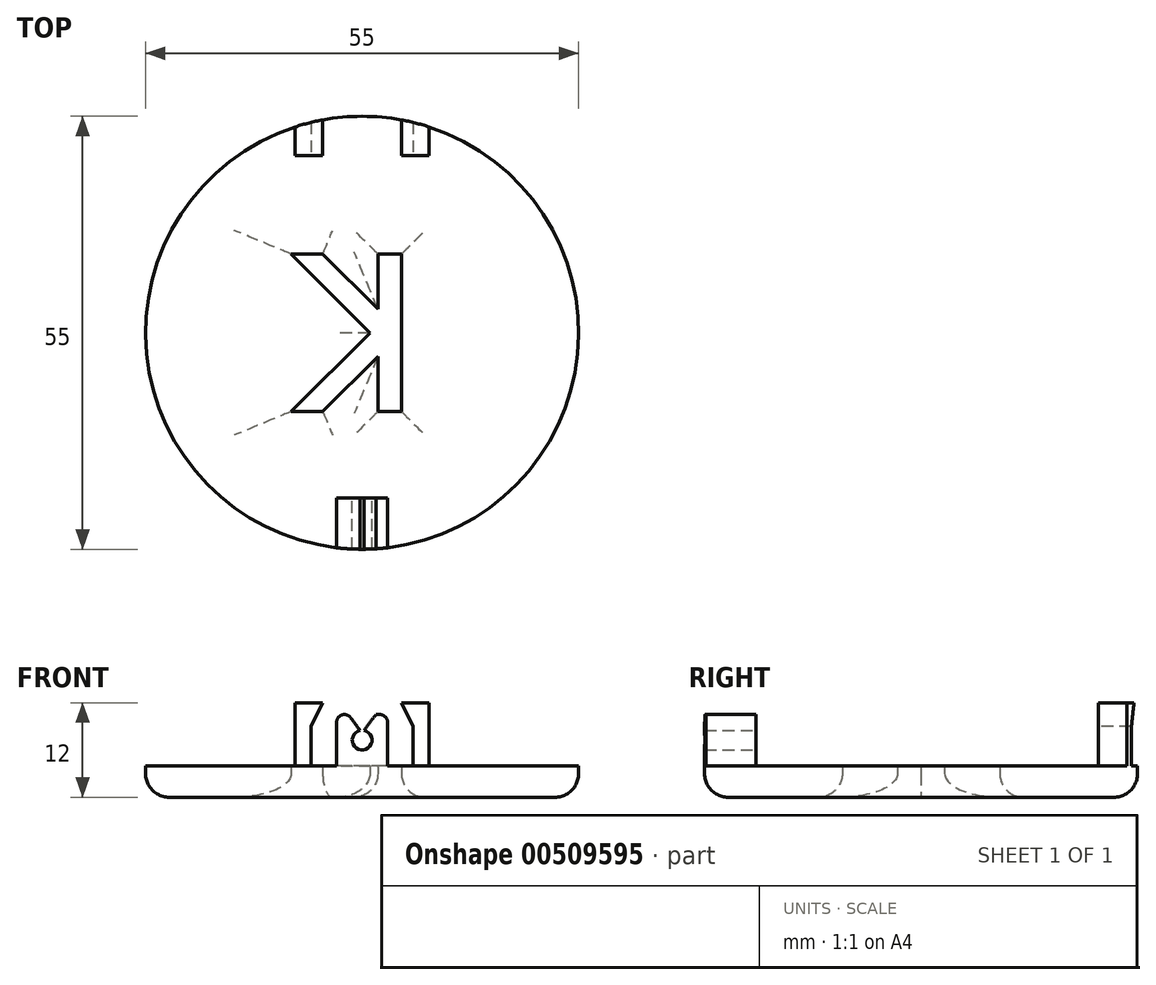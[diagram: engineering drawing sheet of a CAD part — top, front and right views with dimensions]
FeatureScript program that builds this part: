
annotation { "Feature Type Name" : "Feature", "Feature Type Description" : "" }
export const myFeature = defineFeature(function(context is Context, id is Id, definition is map)
    precondition{}
    {
        {
            var Q0;
            Q0=qCreatedBy(makeId("Top.planeOp"),FACE);
            var sketch = newSketch(context, id + "F0", { "sketchPlane" : qUnion([Q0])});
            skCircle(sketch, "E0", {"center": v(0, 0) * mm, "radius": 27.5 * mm});
            skSolve(sketch);
        }
        {
            var Q0;
            Q0=makeQuery(id+"F0.imprint","IMPRINT",FACE,{"disambiguationData":[TD([[makeQuery(id+"F0.imprint","IMPRINT",EDGE,{"derivedFrom":sQuery(id+"F0.wireOp",EDGE,"E0")}),1.0]])]});
            extrude(context, id + "F1", {"entities" : qUnion([Q0]), "depth" : 4 * mm});
        }
        {
            var Q0;
            Q0=makeQuery(id+"F1.opExtrude","CAP_FACE",FACE,{"disambiguationData":[OSD([sQuery(id+"F0.wireOp",EDGE,"E0")])],"isStart":false});
            var sketch = newSketch(context, id + "F2", { "sketchPlane" : qUnion([Q0])});
            skLineSegment(sketch, "E1.bottom", {"start": v(8.5, 27.5) * mm, "end": v(-8.5, 27.5) * mm});
            skLineSegment(sketch, "E1.top", {"start": v(8.5, 22.5) * mm, "end": v(-8.5, 22.5) * mm});
            skLineSegment(sketch, "E1.left", {"start": v(8.5, 27.5) * mm, "end": v(8.5, 22.5) * mm});
            skLineSegment(sketch, "E1.right", {"start": v(-8.5, 27.5) * mm, "end": v(-8.5, 22.5) * mm});
            skPoint(sketch, "E1.middle", {"position": v(0, 25) * mm});
            skSolve(sketch);
        }
        {
            var Q0;
            {var subQ5=sQuery(id+"F2.wireOp",EDGE,"E1.top");Q0=makeQuery(id+"F2.imprint","IMPRINT",FACE,{"disambiguationData":[TD([[makeQuery(id+"F2.imprint","IMPRINT",EDGE,{"derivedFrom":subQ5}),-1.0]])]});}
            extrude(context, id + "F3", {"entities" : qUnion([Q0]), "operationType" : NewBodyOperationType.ADD, "depth" : 8 * mm});
        }
        {
            var Q0;
            Q0=makeQuery(id+"F3.opExtrude","SWEPT_FACE",FACE,{"disambiguationData":[OSD([sQuery(id+"F2.wireOp",EDGE,"E1.top")])]});
            var sketch = newSketch(context, id + "F4", { "sketchPlane" : qUnion([Q0])});
            skLineSegment(sketch, "E2.bottom", {"start": v(6.5, 9) * mm, "end": v(-6.5, 9) * mm});
            skLineSegment(sketch, "E2.top", {"start": v(6.5, 4) * mm, "end": v(-6.5, 4) * mm});
            skLineSegment(sketch, "E2.left", {"start": v(6.5, 9) * mm, "end": v(6.5, 4) * mm});
            skLineSegment(sketch, "E2.right", {"start": v(-6.5, 9) * mm, "end": v(-6.5, 4) * mm});
            skPoint(sketch, "E2.middle", {"position": v(0, 6.5) * mm});
            skSolve(sketch);
        }
        {
            var Q0;
            Q0=makeQuery(id+"F4.imprint","IMPRINT",FACE,{"disambiguationData":[TD([[makeQuery(id+"F4.imprint","IMPRINT",EDGE,{"derivedFrom":sQuery(id+"F4.wireOp",EDGE,"E2.bottom")}),1.0]])]});
            extrude(context, id + "F5", {"entities" : qUnion([Q0]), "operationType" : NewBodyOperationType.REMOVE, "oppositeDirection" : true, "depth" : 25 * mm});
        }
        {
            var Q0;
            Q0=makeQuery(id+"F3.opExtrude","SWEPT_FACE",FACE,{"disambiguationData":[OSD([sQuery(id+"F2.wireOp",EDGE,"E1.top")])]});
            var sketch = newSketch(context, id + "F6", { "sketchPlane" : qUnion([Q0])});
            skLineSegment(sketch, "E3.bottom", {"start": v(5, 12) * mm, "end": v(-5, 12) * mm});
            skLineSegment(sketch, "E3.top", {"start": v(5, 9) * mm, "end": v(-5, 9) * mm});
            skLineSegment(sketch, "E3.left", {"start": v(5, 12) * mm, "end": v(5, 9) * mm});
            skLineSegment(sketch, "E3.right", {"start": v(-5, 12) * mm, "end": v(-5, 9) * mm});
            skPoint(sketch, "E3.middle", {"position": v(0, 10.5) * mm});
            skSolve(sketch);
        }
        {
            var Q0;
            Q0=makeQuery(id+"F6.imprint","IMPRINT",FACE,{"disambiguationData":[TD([[makeQuery(id+"F6.imprint","IMPRINT",EDGE,{"derivedFrom":sQuery(id+"F6.wireOp",EDGE,"E3.bottom")}),1.0]])]});
            extrude(context, id + "F7", {"entities" : qUnion([Q0]), "operationType" : NewBodyOperationType.REMOVE, "oppositeDirection" : true, "depth" : 25 * mm});
        }
        {
            var Q0;
            {var subQ0=sQuery(id+"F2.wireOp",EDGE,"E1.right");var subQ1=sQuery(id+"F2.wireOp",EDGE,"E1.top");Q0=makeQuery(id+"F7.boolean.opBoolean","SPLIT",FACE,{"disambiguationData":[TD([makeQuery(id+"F3.opExtrude","SWEPT_FACE",FACE,{"disambiguationData":[OSD([subQ0])]})])],"derivedFrom":makeQuery(id+"F3.opExtrude","SWEPT_FACE",FACE,{"disambiguationData":[OSD([subQ1])]})});}
            var sketch = newSketch(context, id + "F8", { "sketchPlane" : qUnion([Q0])});
            skLineSegment(sketch, "E4", {"start": v(-6.5, 9) * mm, "end": v(-5, 12) * mm});
            skSolve(sketch);
        }
        {
            var Q0;
            Q0=makeQuery(id+"F8.imprint","IMPRINT",FACE,{"disambiguationData":[TD([[makeQuery(id+"F8.imprint","IMPRINT",EDGE,{"derivedFrom":sQuery(id+"F8.wireOp",EDGE,"E4")}),-1.0]])]});
            extrude(context, id + "F9", {"entities" : qUnion([Q0]), "operationType" : NewBodyOperationType.REMOVE, "oppositeDirection" : true, "depth" : 25 * mm});
        }
        {
            var Q0;
            {var subQ0=sQuery(id+"F2.wireOp",EDGE,"E1.left");var subQ1=sQuery(id+"F2.wireOp",EDGE,"E1.top");Q0=makeQuery(id+"F7.boolean.opBoolean","SPLIT",FACE,{"disambiguationData":[TD([makeQuery(id+"F3.opExtrude","SWEPT_FACE",FACE,{"disambiguationData":[OSD([subQ0])]})])],"derivedFrom":makeQuery(id+"F3.opExtrude","SWEPT_FACE",FACE,{"disambiguationData":[OSD([subQ1])]})});}
            var sketch = newSketch(context, id + "F10", { "sketchPlane" : qUnion([Q0])});
            skLineSegment(sketch, "E5", {"start": v(6.5, 9) * mm, "end": v(5, 12) * mm});
            skSolve(sketch);
        }
        {
            var Q0;
            Q0=makeQuery(id+"F10.imprint","IMPRINT",FACE,{"disambiguationData":[TD([[makeQuery(id+"F10.imprint","IMPRINT",EDGE,{"derivedFrom":sQuery(id+"F10.wireOp",EDGE,"E5")}),1.0]])]});
            extrude(context, id + "F11", {"entities" : qUnion([Q0]), "operationType" : NewBodyOperationType.REMOVE, "oppositeDirection" : true, "depth" : 25 * mm});
        }
        {
            var Q0;
            Q0=makeQuery(id+"F5.boolean.opBoolean","MERGE",FACE,{"derivedFrom":[makeQuery(id+"F1.opExtrude","CAP_FACE",FACE,{"disambiguationData":[OSD([sQuery(id+"F0.wireOp",EDGE,"E0")])],"isStart":false}),makeQuery(id+"F5.opExtrude","SWEPT_FACE",FACE,{"disambiguationData":[OSD([sQuery(id+"F4.wireOp",EDGE,"E2.top")])]})]});
            var sketch = newSketch(context, id + "F12", { "sketchPlane" : qUnion([Q0])});
            skLineSegment(sketch, "E6.bottom", {"start": v(3.25, -21) * mm, "end": v(-3.25, -21) * mm});
            skLineSegment(sketch, "E6.top", {"start": v(3.25, -27.5) * mm, "end": v(-3.25, -27.5) * mm});
            skLineSegment(sketch, "E6.left", {"start": v(3.25, -21) * mm, "end": v(3.25, -27.5) * mm});
            skLineSegment(sketch, "E6.right", {"start": v(-3.25, -21) * mm, "end": v(-3.25, -27.5) * mm});
            skPoint(sketch, "E6.middle", {"position": v(0, -24.25) * mm});
            skPoint(sketch, "E6.middle.positionSnap0", {"position": v(0, -27.5) * mm});
            skPoint(sketch, "E6.centerSnap0", {"position": v(0, -27.5) * mm});
            skSolve(sketch);
        }
        {
            var Q0;
            {var subQ5=sQuery(id+"F12.wireOp",EDGE,"E6.bottom");Q0=makeQuery(id+"F12.imprint","IMPRINT",FACE,{"disambiguationData":[TD([[makeQuery(id+"F12.imprint","IMPRINT",EDGE,{"derivedFrom":subQ5}),1.0]])]});}
            extrude(context, id + "F13", {"entities" : qUnion([Q0]), "operationType" : NewBodyOperationType.ADD, "depth" : 6.5 * mm});
        }
        {
            var Q0;
            Q0=makeQuery(id+"F13.opExtrude","SWEPT_FACE",FACE,{"disambiguationData":[OSD([sQuery(id+"F12.wireOp",EDGE,"E6.bottom")])]});
            var sketch = newSketch(context, id + "F14", { "sketchPlane" : qUnion([Q0])});
            skPoint(sketch, "E7", {"position": v(0, 7.25) * mm});
            skSolve(sketch);
        }
        {
            var Q0;
            Q0=sQuery(id+"F14.wireOp",VERTEX,"E7");
            var Q1;
            Q1=makeQuery(id+"F1.opExtrude","SWEPT_BODY",BODY,{"disambiguationData":[OSD([sQuery(id+"F0.wireOp",EDGE,"E0")])]});
            hole(context, id + "F15", {"style" : HoleStyle.SIMPLE, "endStyle" : HoleEndStyle.THROUGH, "holeDiameter" : 2.5 * mm, "isTappedThrough" : true, "tappedDepth" : 12 * mm, "tapClearance" : 3, "locations" : qUnion([Q0]), "scope" : qUnion([Q1])});
        }
        {
            var Q0;
            Q0=makeQuery(id+"F13.opExtrude","SWEPT_FACE",FACE,{"disambiguationData":[OSD([sQuery(id+"F12.wireOp",EDGE,"E6.bottom")])]});
            var sketch = newSketch(context, id + "F16", { "sketchPlane" : qUnion([Q0])});
            skLineSegment(sketch, "E8", {"start": v(-0.25, 8.47) * mm, "end": v(-1.75, 10.5) * mm});
            skLineSegment(sketch, "E9", {"start": v(0.25, 8.47) * mm, "end": v(1.75, 10.5) * mm});
            skSolve(sketch);
        }
        {
            var Q0;
            {var subQ0=sQuery(id+"F16.wireOp",EDGE,"E8");Q0=makeQuery(id+"F16.imprint","IMPRINT",FACE,{"disambiguationData":[TD([[makeQuery(id+"F16.imprint","IMPRINT",EDGE,{"derivedFrom":subQ0}),-1.0]])]});}
            extrude(context, id + "F17", {"entities" : qUnion([Q0]), "operationType" : NewBodyOperationType.REMOVE, "oppositeDirection" : true, "depth" : 25 * mm});
        }
        {
            var Q0;
            Q0=makeQuery(id+"F17.boolean.opBoolean","COPY",EDGE,{"derivedFrom":makeQuery(id+"F17.opExtrude","SWEPT_EDGE",EDGE,{"disambiguationData":[OSD([sQuery(id+"F15.hole-0.sketch.wireOp",EDGE,"core_line_2"),sQuery(id+"F15.hole-0.sketch.wireOp",EDGE,"core_line_3"),sQuery(id+"F16.wireOp",EDGE,"E8")])]})});
            var Q1;
            Q1=makeQuery(id+"F17.boolean.opBoolean","COPY",EDGE,{"derivedFrom":makeQuery(id+"F17.opExtrude","SWEPT_EDGE",EDGE,{"disambiguationData":[OSD([sQuery(id+"F15.hole-0.sketch.wireOp",EDGE,"core_line_2"),sQuery(id+"F15.hole-0.sketch.wireOp",EDGE,"core_line_3"),sQuery(id+"F16.wireOp",EDGE,"E9")])]})});
            fillet(context, id + "F18", {"entities" : qUnion([Q0, Q1]), "radius" : 1 * mm, "tangentPropagation" : true, "allowEdgeOverflow" : false});
        }
        {
            var Q0;
            Q0=makeQuery(id+"F13.opExtrude","CAP_EDGE",EDGE,{"disambiguationData":[OSD([sQuery(id+"F12.wireOp",EDGE,"E6.left")])],"isStart":false});
            var Q1;
            Q1=makeQuery(id+"F13.opExtrude","CAP_EDGE",EDGE,{"disambiguationData":[OSD([sQuery(id+"F12.wireOp",EDGE,"E6.right")])],"isStart":false});
            var Q2;
            Q2=makeQuery(id+"F17.boolean.opBoolean","COPY",EDGE,{"derivedFrom":makeQuery(id+"F17.opExtrude","SWEPT_EDGE",EDGE,{"disambiguationData":[OSD([sQuery(id+"F12.wireOp",EDGE,"E6.bottom"),sQuery(id+"F16.wireOp",EDGE,"E8")])]})});
            var Q3;
            Q3=makeQuery(id+"F17.boolean.opBoolean","COPY",EDGE,{"derivedFrom":makeQuery(id+"F17.opExtrude","SWEPT_EDGE",EDGE,{"disambiguationData":[OSD([sQuery(id+"F12.wireOp",EDGE,"E6.bottom"),sQuery(id+"F16.wireOp",EDGE,"E9")])]})});
            fillet(context, id + "F19", {"entities" : qUnion([Q0, Q1, Q2, Q3]), "radius" : 1 * mm, "tangentPropagation" : true, "allowEdgeOverflow" : false});
        }
        {
            var Q0;
            Q0=makeQuery(id+"F1.opExtrude","CAP_FACE",FACE,{"disambiguationData":[OSD([sQuery(id+"F0.wireOp",EDGE,"E0")])],"isStart":true});
            var sketch = newSketch(context, id + "F20", { "sketchPlane" : qUnion([Q0])});
            skLineSegment(sketch, "E10", {"start": v(5, -10) * mm, "end": v(5, 10) * mm});
            skLineSegment(sketch, "E11", {"start": v(5, 10) * mm, "end": v(2, 10) * mm});
            skLineSegment(sketch, "E12", {"start": v(2, 10) * mm, "end": v(2, 3) * mm});
            skLineSegment(sketch, "E13", {"start": v(2, 3) * mm, "end": v(-5, 10) * mm});
            skLineSegment(sketch, "E14", {"start": v(-5, 10) * mm, "end": v(-9, 10) * mm});
            skLineSegment(sketch, "E15", {"start": v(-9, 10) * mm, "end": v(1, 0) * mm});
            skLineSegment(sketch, "E16", {"start": v(1, 0) * mm, "end": v(-9, -10) * mm});
            skLineSegment(sketch, "E17", {"start": v(-9, -10) * mm, "end": v(-5, -10) * mm});
            skLineSegment(sketch, "E18", {"start": v(-5, -10) * mm, "end": v(2, -3) * mm});
            skLineSegment(sketch, "E19", {"start": v(2, -3) * mm, "end": v(2, -10) * mm});
            skLineSegment(sketch, "E20", {"start": v(2, -10) * mm, "end": v(5, -10) * mm});
            skSolve(sketch);
        }
        {
            var Q0;
            Q0=makeQuery(id+"F20.imprint","IMPRINT",FACE,{"disambiguationData":[TD([[makeQuery(id+"F20.imprint","IMPRINT",EDGE,{"derivedFrom":sQuery(id+"F20.wireOp",EDGE,"E10")}),1.0]])]});
            extrude(context, id + "F21", {"entities" : qUnion([Q0]), "operationType" : NewBodyOperationType.REMOVE, "oppositeDirection" : true, "depth" : 25 * mm});
        }
        {
            var Q0;
            Q0=makeQuery(id+"F1.opExtrude","CAP_FACE",FACE,{"disambiguationData":[OSD([sQuery(id+"F0.wireOp",EDGE,"E0")])],"isStart":true});
            fillet(context, id + "F22", {"entities" : qUnion([Q0]), "radius" : 3 * mm, "tangentPropagation" : true, "allowEdgeOverflow" : false});
        }
    });
